FCSTD DOCUMENT  (FreeCAD 0.19R24348 (Git))
Label: ThirdTry
License: All rights reserved
LicenseURL: http://en.wikipedia.org/wiki/All_rights_reserved
objects: Sketcher::SketchObject×3, Spreadsheet::Sheet×1
note: 3 computed .brp shape members not serialized (recipe doc carries the construction recipe); baked Part::Feature solids carry a one-line shape summary decoded from their .brp

FEATURE [Sketcher::SketchObject] Sketch
  FullyConstrained = true
  expr: Constraints[2] = <<Parameters>>.RW_1
  expr: Constraints[1] = <<Parameters>>.RW_2
  expr: Constraints[39] = <<Parameters>>.FW_1
  expr: Constraints[36] = <<Parameters>>.FW_2
  expr: Constraints[50] = <<Parameters>>.WX_1
  expr: Constraints[4] = <<Parameters>>.WY_1
  expr: Constraints[32] = <<Parameters>>.RW_4
  expr: Constraints[31] = <<Parameters>>.RW_3
  expr: Constraints[21] = <<Parameters>>.RW_6
  expr: Constraints[55] = 180 - <<Parameters>>.KAT
  expr: Constraints[22] = <<Parameters>>.RW_5
  expr: Constraints[16] = <<Parameters>>.WX_1
  expr: Constraints[20] = <<Parameters>>.WX_2
  sketch-geometry (21):
    g0: ArcOfCircle CenterX=0 CenterY=106 CenterZ=0 NormalX=0 NormalY=0 NormalZ=1 AngleXU=0 Radius=14 StartAngle=0.304693 EndAngle=4.4077
    g1: ArcOfCircle CenterX=-6 CenterY=86.9212 CenterZ=0 NormalX=0 NormalY=0 NormalZ=1 AngleXU=0 Radius=6 StartAngle=1e-16 EndAngle=1.2661
    g2: ArcOfCircle CenterX=19.0788 CenterY=112 CenterZ=0 NormalX=0 NormalY=0 NormalZ=1 AngleXU=0 Radius=6 StartAngle=3.44629 EndAngle=4.71239
    g3: LineSegment StartX=0 StartY=106 StartZ=0 EndX=0 EndY=0 EndZ=0
    g4: LineSegment StartX=0 StartY=106 StartZ=0 EndX=136 EndY=106 EndZ=0
    g5: LineSegment StartX=19.0788 StartY=106 StartZ=0 EndX=106 EndY=106 EndZ=0
    g6: LineSegment StartX=0 StartY=0 StartZ=0 EndX=106 EndY=0 EndZ=0
    g7: ArcOfCircle CenterX=106 CenterY=13 CenterZ=0 NormalX=0 NormalY=0 NormalZ=1 AngleXU=0 Radius=13 StartAngle=4.71239 EndAngle=6.28319
    g8: ArcOfCircle CenterX=125 CenterY=13 CenterZ=0 NormalX=0 NormalY=0 NormalZ=1 AngleXU=0 Radius=6 StartAngle=1.5708 EndAngle=3.14159
    g9: LineSegment StartX=136 StartY=106 StartZ=0 EndX=136 EndY=19 EndZ=0
    g10: LineSegment StartX=125 StartY=19 StartZ=0 EndX=136 EndY=19 EndZ=0
    g11: ArcOfCircle CenterX=106 CenterY=79 CenterZ=0 NormalX=0 NormalY=0 NormalZ=1 AngleXU=0 Radius=27 StartAngle=1.32645 EndAngle=1.5708
    g12: ArcOfCircle CenterX=130 CenterY=94.659 CenterZ=0 NormalX=0 NormalY=0 NormalZ=1 AngleXU=0 Radius=6 StartAngle=3.01619e-08 EndAngle=1.32645
    g13: LineSegment StartX=106 StartY=13 StartZ=0 EndX=125 EndY=13 EndZ=0
    g14: LineSegment StartX=136 StartY=22.8891 StartZ=0 EndX=132.111 EndY=19 EndZ=0
    g15: LineSegment StartX=0 StartY=4.24264 StartZ=0 EndX=4.24264 EndY=0 EndZ=0
    g16: LineSegment StartX=132.111 StartY=19 StartZ=0 EndX=125 EndY=19 EndZ=0
    g17: LineSegment StartX=136 StartY=94.659 StartZ=0 EndX=136 EndY=22.8891 EndZ=0
    g18: LineSegment StartX=0 StartY=86.9212 StartZ=0 EndX=0 EndY=4.24264 EndZ=0
    g19: LineSegment StartX=4.24264 StartY=0 StartZ=0 EndX=106 EndY=0 EndZ=0
    g20: LineSegment StartX=112.532 StartY=105.198 StartZ=0 EndX=131.452 EndY=100.481 EndZ=0
  constraints (60):
    c: Equal(g2,g1)
    c: Radius(g0) = 14
    c: Radius(g1) = 6
    c: Vertical(g3)
    c: DistanceY(g3,g3) = 106
    c: Coincident(g4,g0)
    c: Horizontal(g4)
    c: Coincident(g0,g3)
    c: Tangent(g1,g3) = 1.5708
    c: Tangent(g2,g4) = -1.5708
    c: Tangent(g0,g1) = 1.5708
    c: Tangent(g0,g2) = 1.5708
    c: Coincident(g5,g2)
    c: Coincident(g3,g-1)
    c: Coincident(g6,g-1)
    c: Horizontal(g6)
    c: DistanceX(g6,g6) = 106
    c: Vertical(g9)
    c: Horizontal(g10)
    c: Horizontal(g5)
    c: DistanceX(g4,g4) = 136
    c: Radius(g7) = 13
    c: Radius(g8) = 6
    c: Horizontal(g13)
    c: Coincident(g10,g9)
    c: Coincident(g13,g7)
    c: Coincident(g13,g8)
    c: Tangent(g7,g6) = -1.5708
    c: Tangent(g8,g7) = 1.5708
    c: Coincident(g10,g8)
    c: Tangent(g10,g8)
    c: Radius(g11) = 27
    c: Radius(g12) = 6
    c: PointOnObject(g14,g9)
    c: PointOnObject(g14,g10)
    c: Angle(g14,g10) = 2.35619
    c: Distance(g14) = 5.5
    c: PointOnObject(g15,g3)
    c: PointOnObject(g15,g6)
    c: Distance(g15) = 6
    c: Angle(g15,g3) = 2.35619
    c: Coincident(g16,g14)
    c: Coincident(g16,g8)
    c: Coincident(g17,g12)
    c: Coincident(g17,g14)
    c: Coincident(g18,g1)
    c: Coincident(g18,g15)
    c: Coincident(g19,g15)
    c: Coincident(g19,g7)
    c: Coincident(g9,g4)
    c: DistanceX(g0,g5) = 106
    c: Tangent(g12,g9)
    c: Parallel(g17,g9)
    c: Coincident(g20,g12)
    c: Tangent(g12,g20)
    c: Angle(g4,g20) = 2.89725
    c: Coincident(g20,g11)
    c: Coincident(g11,g5)
    c: Tangent(g11,g4)
    c: Tangent(g11,g20)
FEATURE [Spreadsheet::Sheet] Spreadsheet  label="Parameters"
  cells = A1=D_1; B1(D_1)=27; A2=KAT; B2(KAT)=14; A3=KAT_2; B3(KAT_2)=28; A4=KPX; B4(KPX)=69; A5=KPY; B5(KPY)=45; A6=D_2; B6(D_2)=39; A7=RKK_1; B7(RKK_1)=6; A8=KOX; B8(KOX)=53; A9=KOY; B9(KOY)=53; A10=WX_1; B10(WX_1)=106; A11=WX_2; B11(WX_2)=136; A12=WY_1; B12(WY_1)=106; A13=RW_1; B13(RW_1)=6; A14=RW_2; B14(RW_2)=14; A15=RW_3; B15(RW_3)=27; A16=RW_4; B16(RW_4)=6; A17=RW_5; B17(RW_5)=6; A18=RW_6; B18(RW_6)=13; A19=FW_1; B19(FW_1)=6; A20=FW_2; B20(FW_2)=5.5; A21=KX_1; B21(KX_1)=12; A22=KX_2; B22(KX_2)=17; A23=KX_3; B23(KX_3)=68; A24=KX_4; B24(KX_4)=139; A25=KX_5; B25(KX_5)=168; A26=KX_6; B26(KX_6)=180; A27=KY_1; B27(KY_1)=12; A28=KY_2; B28(KY_2)=38; A29=KY_3; B29(KY_3)=109; A30=KY_4; B30(KY_4)=146; A31=KY_5; B31(KY_5)=154; A32=KY_6; B32(KY_6)=166; A33=FK_1; B33(FK_1)=2; A34=RK_1; B34(RK_1)=2; A35=H_1; B35(H_1)=12; A36=H_2; B36(H_2)=18; A37=KH_1; B37(KH_1)=10; A38=KH_2; B38(KH_2)=6; A39=OTWX_1; B39(OTWX_1)=9; A40=OTWY_1; B40(OTWY_1)=7; A41=OTWY_2; B41(OTWY_2)=14; A42=GOTW_1; B42(GOTW_1)=14; A43=GOTW_2; B43(GOTW_2)=10; A44=WY_1_1; B44(WY_1_1)=19.0787840283389
FEATURE [Sketcher::SketchObject] Sketch001  label="Srodek"
  FullyConstrained = true
  MapMode = 2
  Support = -> [Sketch]
  expr: Constraints[50] = <<Parameters>>.KPX
  expr: Constraints[43] = <<Parameters>>.RKK_1
  expr: Constraints[51] = <<Parameters>>.KPY
  expr: Constraints[21] = <<Parameters>>.D_1
  expr: Constraints[20] = <<Parameters>>.D_2
  expr: Constraints[10] = <<Parameters>>.KOY
  expr: Constraints[55] = <<Parameters>>.KAT_2
  expr: Constraints[9] = <<Parameters>>.KOX
  sketch-geometry (29):
    g0: LineSegment StartX=0 StartY=0 StartZ=0 EndX=53 EndY=0 EndZ=0
    g1: LineSegment StartX=53 StartY=0 StartZ=0 EndX=53 EndY=53 EndZ=0
    g2: LineSegment StartX=53 StartY=53 StartZ=0 EndX=0 EndY=53 EndZ=0
    g3: LineSegment StartX=0 StartY=53 StartZ=0 EndX=0 EndY=0 EndZ=0
    g4: Circle CenterX=53 CenterY=53 CenterZ=0 NormalX=0 NormalY=0 NormalZ=1 AngleXU=0 Radius=13.5
    g5: Circle CenterX=53 CenterY=53 CenterZ=0 NormalX=0 NormalY=0 NormalZ=1 AngleXU=0 Radius=19.5
    g6: Circle CenterX=34.3521 CenterY=58.7012 CenterZ=0 NormalX=0 NormalY=0 NormalZ=1 AngleXU=0 Radius=2.5
    g7: Circle CenterX=58.7012 CenterY=71.6479 CenterZ=0 NormalX=0 NormalY=0 NormalZ=1 AngleXU=0 Radius=2.5
    g8: Circle CenterX=71.6479 CenterY=47.2988 CenterZ=0 NormalX=0 NormalY=0 NormalZ=1 AngleXU=0 Radius=2.5
    g9: Circle CenterX=47.2988 CenterY=34.3521 CenterZ=0 NormalX=0 NormalY=0 NormalZ=1 AngleXU=0 Radius=2.5
    g10: LineSegment StartX=53 StartY=53 StartZ=0 EndX=34.3521 EndY=58.7012 EndZ=0
    g11: LineSegment StartX=47.2988 StartY=34.3521 StartZ=0 EndX=53 EndY=53 EndZ=0
    g12: LineSegment StartX=71.6479 StartY=47.2988 StartZ=0 EndX=53 EndY=53 EndZ=0
    g13: LineSegment StartX=58.7012 StartY=71.6479 StartZ=0 EndX=53 EndY=53 EndZ=0
    g14: LineSegment StartX=34.3521 StartY=58.7012 StartZ=0 EndX=58.7012 EndY=71.6479 EndZ=0
    g15: LineSegment StartX=47.2988 StartY=34.3521 StartZ=0 EndX=71.6479 EndY=47.2988 EndZ=0
    g16: LineSegment StartX=9.15837 StartY=61.9672 StartZ=0 EndX=70.0818 EndY=94.3608 EndZ=0
    g17: LineSegment StartX=78.1963 StartY=91.8799 StartZ=0 EndX=99.3225 EndY=52.1473 EndZ=0
    g18: LineSegment StartX=96.8416 StartY=44.0328 StartZ=0 EndX=35.9182 EndY=11.6392 EndZ=0
    g19: LineSegment StartX=27.8037 StartY=14.1201 StartZ=0 EndX=6.67751 EndY=53.8527 EndZ=0
    g20: ArcOfCircle CenterX=11.9752 CenterY=56.6696 CenterZ=0 NormalX=0 NormalY=0 NormalZ=1 AngleXU=0 Radius=6 StartAngle=2.05949 EndAngle=3.63028
    g21: ArcOfCircle CenterX=72.8986 CenterY=89.0631 CenterZ=0 NormalX=0 NormalY=0 NormalZ=1 AngleXU=0 Radius=6 StartAngle=0.488692 EndAngle=2.05949
    g22: ArcOfCircle CenterX=94.0248 CenterY=49.3304 CenterZ=0 NormalX=0 NormalY=0 NormalZ=1 AngleXU=0 Radius=6 StartAngle=5.20108 EndAngle=6.77188
    g23: ArcOfCircle CenterX=33.1014 CenterY=16.9369 CenterZ=0 NormalX=0 NormalY=0 NormalZ=1 AngleXU=0 Radius=6 StartAngle=3.63028 EndAngle=5.20108
    g24: LineSegment StartX=17.2406 StartY=33.9864 StartZ=0 EndX=53 EndY=53 EndZ=0
    g25: LineSegment StartX=9.15837 StartY=61.9672 StartZ=0 EndX=39.6201 EndY=78.164 EndZ=0
    g26: LineSegment StartX=39.6201 StartY=78.164 StartZ=0 EndX=53 EndY=53 EndZ=0
    g27: LineSegment StartX=66.3799 StartY=27.836 StartZ=0 EndX=53 EndY=53 EndZ=0
    g28: LineSegment StartX=53 StartY=53 StartZ=0 EndX=88.7594 EndY=72.0136 EndZ=0
  constraints (73):
    c: Coincident(g0,g1)
    c: Coincident(g1,g2)
    c: Coincident(g2,g3)
    c: Coincident(g3,g0)
    c: Horizontal(g0)
    c: Horizontal(g2)
    c: Vertical(g1)
    c: Vertical(g3)
    c: Coincident(g0,g-1)
    c: DistanceX(g2,g2) = 53
    c: DistanceY(g1,g1) = 53
    c: Coincident(g4,g1)
    c: Coincident(g5,g4)
    c: PointOnObject(g6,g5)
    c: PointOnObject(g7,g5)
    c: PointOnObject(g8,g5)
    c: PointOnObject(g9,g5)
    c: Equal(g9,g6)
    c: Equal(g6,g7)
    c: Equal(g7,g8)
    c: Diameter(g5) = 39
    c: Diameter(g4) = 27
    c: Coincident(g10,g4)
    c: Coincident(g10,g6)
    c: Coincident(g11,g9)
    c: Coincident(g11,g4)
    c: Coincident(g12,g8)
    c: Coincident(g12,g4)
    c: Coincident(g13,g7)
    c: Coincident(g13,g4)
    c: Angle(g10,g11) = 1.5708
    c: Angle(g13,g10) = 1.5708
    c: Angle(g12,g13) = 1.5708
    c: Diameter(g7) = 5
    c: Coincident(g14,g6)
    c: Coincident(g14,g7)
    c: Coincident(g15,g9)
    c: Coincident(g15,g8)
    c: Equal(g20,g23)
    c: Equal(g23,g22)
    c: Equal(g22,g21)
    c: Tangent(g20,g16) = 1.5708
    c: Tangent(g20,g19) = 1.5708
    c: Radius(g20) = 6
    c: Tangent(g17,g21) = 1.5708
    c: Tangent(g16,g21) = 1.5708
    c: Tangent(g22,g18) = 1.5708
    c: Tangent(g22,g17) = 1.5708
    c: Tangent(g19,g23) = 1.5708
    c: Tangent(g18,g23) = 1.5708
    c: Distance(g16,g16) = 69
    c: Distance(g19,g19) = 45
    c: Parallel(g16,g18)
    c: Parallel(g19,g17)
    c: Perpendicular(g18,g19)
    c: Angle(g0,g18) = 0.488692
    c: Parallel(g15,g18)
    c: PointOnObject(g24,g19)
    c: Coincident(g24,g4)
    c: PointOnObject(g25,g16)
    c: Parallel(g24,g16)
    c: Coincident(g25,g16)
    c: Coincident(g26,g25)
    c: Coincident(g26,g4)
    c: PointOnObject(g27,g18)
    c: Coincident(g27,g4)
    c: Perpendicular(g18,g27)
    c: Perpendicular(g16,g26)
    c: Coincident(g28,g4)
    c: PointOnObject(g28,g17)
    c: Perpendicular(g17,g28)
    c: Equal(g24,g28)
    c: Equal(g27,g26)
FEATURE [Sketcher::SketchObject] Sketch002  label="Ramka"
  FullyConstrained = true
  MapMode = 2
  Support = -> [Sketch001]
  expr: Constraints[9] = <<Parameters>>.KY_6
  expr: Constraints[10] = <<Parameters>>.KX_6
  expr: Constraints[18] = <<Parameters>>.FW_1
  expr: Constraints[50] = <<Parameters>>.KY_6 - <<Parameters>>.KY_5
  expr: Constraints[47] = <<Parameters>>.KX_1
  expr: Constraints[59] = <<Parameters>>.RK_1
  expr: Constraints[48] = <<Parameters>>.KX_6 - <<Parameters>>.KX_5
  expr: Constraints[49] = <<Parameters>>.KY_1
  sketch-geometry (24):
    g0: LineSegment StartX=0 StartY=0 StartZ=0 EndX=180 EndY=0 EndZ=0
    g1: LineSegment StartX=180 StartY=0 StartZ=0 EndX=180 EndY=166 EndZ=0
    g2: LineSegment StartX=180 StartY=166 StartZ=0 EndX=0 EndY=166 EndZ=0
    g3: LineSegment StartX=0 StartY=166 StartZ=0 EndX=0 EndY=0 EndZ=0
    g4: ArcOfCircle CenterX=2 CenterY=164 CenterZ=0 NormalX=0 NormalY=0 NormalZ=1 AngleXU=0 Radius=2 StartAngle=1.5708 EndAngle=3.14159
    g5: ArcOfCircle CenterX=178 CenterY=2 CenterZ=0 NormalX=0 NormalY=0 NormalZ=1 AngleXU=0 Radius=2 StartAngle=4.71239 EndAngle=6.28319
    g6: LineSegment StartX=0 StartY=4.24264 StartZ=0 EndX=4.24264 EndY=0 EndZ=0
    g7: LineSegment StartX=0 StartY=164 StartZ=0 EndX=0 EndY=4.24264 EndZ=0
    g8: LineSegment StartX=178 StartY=0 StartZ=0 EndX=4.24264 EndY=0 EndZ=0
    g9: LineSegment StartX=175.757 StartY=166 StartZ=0 EndX=180 EndY=161.757 EndZ=0
    g10: LineSegment StartX=2 StartY=166 StartZ=0 EndX=175.757 EndY=166 EndZ=0
    g11: LineSegment StartX=180 StartY=2 StartZ=0 EndX=180 EndY=161.757 EndZ=0
    g12: Circle CenterX=12 CenterY=154 CenterZ=0 NormalX=0 NormalY=0 NormalZ=1 AngleXU=0 Radius=3.3
    g13: Circle CenterX=12 CenterY=154 CenterZ=0 NormalX=0 NormalY=0 NormalZ=1 AngleXU=0 Radius=6.72
    g14: Circle CenterX=168 CenterY=154 CenterZ=0 NormalX=0 NormalY=0 NormalZ=1 AngleXU=0 Radius=3.3
    g15: Circle CenterX=168 CenterY=154 CenterZ=0 NormalX=0 NormalY=0 NormalZ=1 AngleXU=0 Radius=6.72
    g16: Circle CenterX=168 CenterY=12 CenterZ=0 NormalX=0 NormalY=0 NormalZ=1 AngleXU=0 Radius=3.3
    g17: Circle CenterX=168 CenterY=12 CenterZ=0 NormalX=0 NormalY=0 NormalZ=1 AngleXU=0 Radius=6.72
    g18: Circle CenterX=12 CenterY=12 CenterZ=0 NormalX=0 NormalY=0 NormalZ=1 AngleXU=0 Radius=3.3
    g19: Circle CenterX=12 CenterY=12 CenterZ=0 NormalX=0 NormalY=0 NormalZ=1 AngleXU=0 Radius=6.72
    g20: LineSegment StartX=12 StartY=12 StartZ=0 EndX=168 EndY=12 EndZ=0
    g21: LineSegment StartX=12 StartY=154 StartZ=0 EndX=168 EndY=154 EndZ=0
    g22: LineSegment StartX=168 StartY=154 StartZ=0 EndX=168 EndY=12 EndZ=0
    g23: LineSegment StartX=12 StartY=12 StartZ=0 EndX=12 EndY=154 EndZ=0
  constraints (61):
    c: Coincident(g0,g1)
    c: Coincident(g1,g2)
    c: Coincident(g2,g3)
    c: Coincident(g3,g0)
    c: Horizontal(g0)
    c: Horizontal(g2)
    c: Vertical(g1)
    c: Vertical(g3)
    c: Coincident(g0,g-1)
    c: DistanceY(g3,g3) = 166
    c: DistanceX(g2,g2) = 180
    c: Equal(g4,g5)
    c: Tangent(g4,g2) = -1.5708
    c: Tangent(g4,g3) = -1.5708
    c: Tangent(g5,g0) = -1.5708
    c: Tangent(g5,g1) = -1.5708
    c: PointOnObject(g6,g3)
    c: PointOnObject(g6,g0)
    c: Distance(g6) = 6
    c: Angle(g0,g6) = 2.35619
    c: Coincident(g7,g4)
    c: Coincident(g7,g6)
    c: Coincident(g8,g5)
    c: Coincident(g8,g6)
    c: PointOnObject(g9,g2)
    c: PointOnObject(g9,g1)
    c: Equal(g9,g6)
    c: Coincident(g10,g4)
    c: Coincident(g10,g9)
    c: Coincident(g11,g5)
    c: Coincident(g11,g9)
    c: Coincident(g13,g12)
    c: Coincident(g15,g14)
    c: Coincident(g17,g16)
    c: Coincident(g19,g18)
    c: Coincident(g20,g18)
    c: Coincident(g20,g16)
    c: Coincident(g21,g12)
    c: Coincident(g21,g14)
    c: Horizontal(g21)
    c: Coincident(g22,g14)
    c: Coincident(g22,g16)
    c: Coincident(g23,g18)
    c: Coincident(g23,g12)
    c: Vertical(g23)
    c: Horizontal(g20)
    c: Vertical(g22)
    c: DistanceX(g-1,g18) = 12
    c: DistanceX(g16,g0) = 12
    c: DistanceY(g-1,g18) = 12
    c: DistanceY(g12,g2) = 12
    c: Equal(g15,g17)
    c: Equal(g17,g19)
    c: Equal(g19,g13)
    c: Equal(g12,g14)
    c: Equal(g14,g18)
    c: Equal(g18,g16)
    c: Diameter(g15) = 13.44
    c: Diameter(g14) = 6.6
    c: Radius(g4) = 2
    c: Angle(g9,g1) = 2.35619
